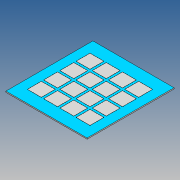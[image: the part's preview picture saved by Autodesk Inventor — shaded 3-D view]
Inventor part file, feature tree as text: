
AUTODESK INVENTOR PART (.ipt)
format: ipt  version: 2017 (Build 210142000, 142)  size: 169,984 bytes
history: native  units: mm
features: extrude x2, sketch x2, other x1
ambient origin geometry x8: Origin, YZ Plane, XZ Plane, XY Plane, X Axis, Y Axis, Z Axis, Center Point
bodies: Body1 (feature_tree)
feature tree (5):
  other  "Sólido1"
  extrude  "Extrusión1"  Depth=75.0mm
  extrude  "Extrusión2"  Depth=40.0mm
  sketch  "Boceto1"  dims[d0=70.0mm d1=75.0mm]
  sketch  "Boceto2"  dims[d2=1.0mm d3=0.0mm d4=40.0mm d6=14.0mm d7=40.0mm d9=14.0mm d12=12.0mm d13=0.1mm d14=0.0mm]
